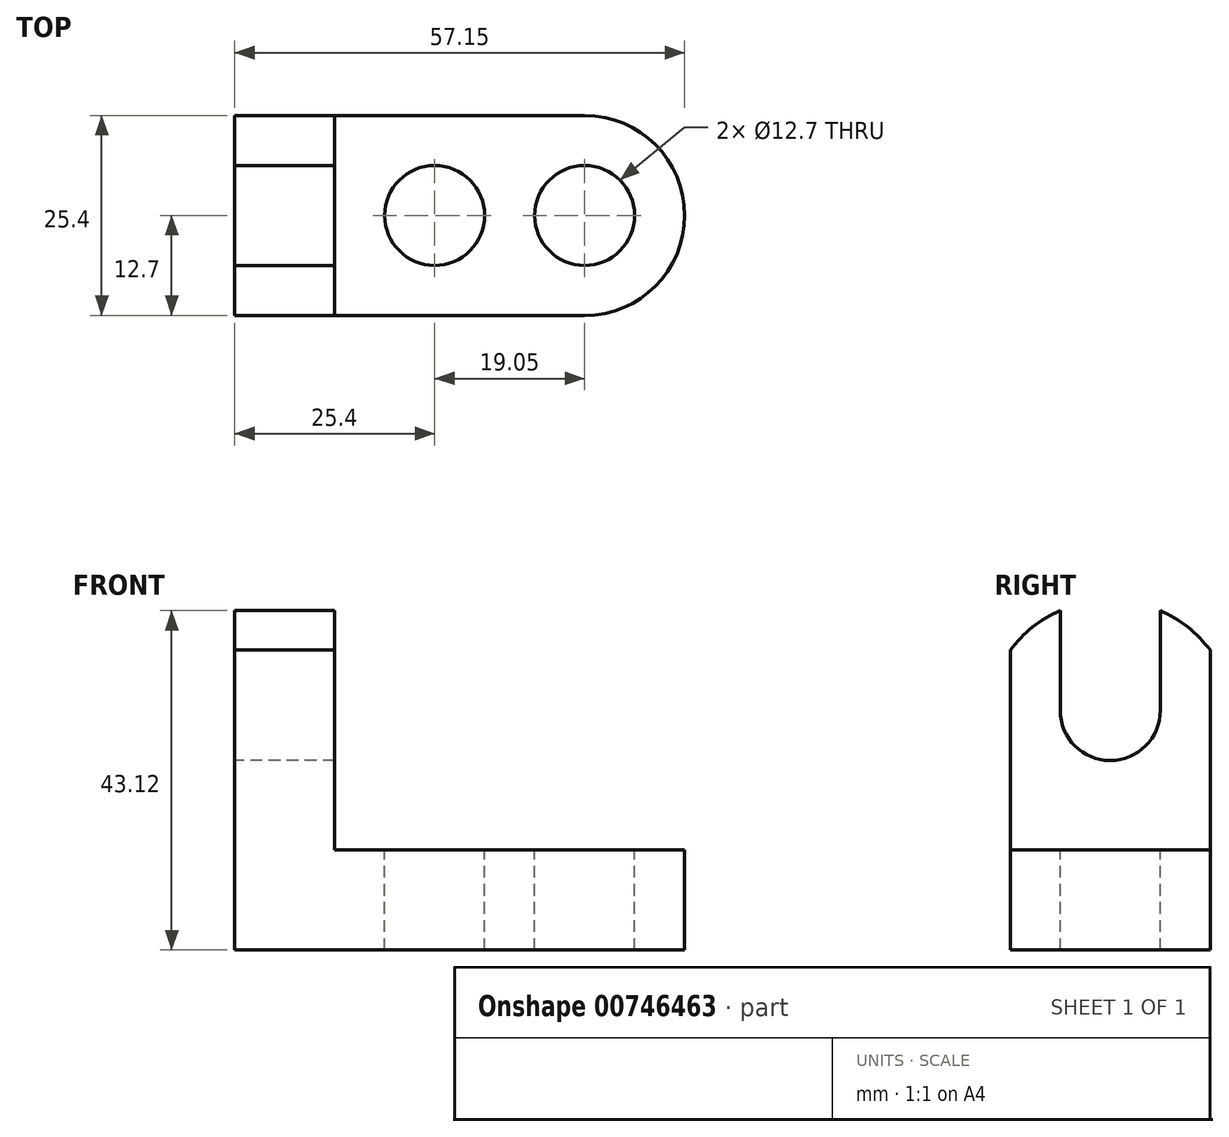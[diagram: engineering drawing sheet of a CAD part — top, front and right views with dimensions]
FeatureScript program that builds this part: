
annotation { "Feature Type Name" : "Feature", "Feature Type Description" : "" }
export const myFeature = defineFeature(function(context is Context, id is Id, definition is map)
    precondition{}
    {
        {
            var Q0;
            Q0=qCreatedBy(makeId("Front.planeOp"),FACE);
            var sketch = newSketch(context, id + "F0", { "sketchPlane" : qUnion([Q0])});
            skLineSegment(sketch, "E0", {"start": v(0, 0) * mm, "end": v(44.45, 0) * mm});
            skLineSegment(sketch, "E1", {"start": v(44.45, 0) * mm, "end": v(44.45, 12.7) * mm});
            skLineSegment(sketch, "E2", {"start": v(44.45, 12.7) * mm, "end": v(12.7, 12.7) * mm});
            skLineSegment(sketch, "E3", {"start": v(12.7, 12.7) * mm, "end": v(12.7, 38.1) * mm});
            skLineSegment(sketch, "E4", {"start": v(12.7, 38.1) * mm, "end": v(0, 38.1) * mm});
            skLineSegment(sketch, "E5", {"start": v(0, 38.1) * mm, "end": v(0, 0) * mm});
            skSolve(sketch);
        }
        {
            var Q0;
            Q0=makeQuery(id+"F0.imprint","IMPRINT",FACE,{"disambiguationData":[TD([[makeQuery(id+"F0.imprint","IMPRINT",EDGE,{"derivedFrom":sQuery(id+"F0.wireOp",EDGE,"E0")}),1.0]])]});
            extrude(context, id + "F1", {"entities" : qUnion([Q0]), "depth" : 25.4 * mm, "offsetDistance" : 25.4 * mm});
        }
        {
            var Q0;
            Q0=makeQuery(id+"F1.opExtrude","SWEPT_FACE",FACE,{"disambiguationData":[OSD([sQuery(id+"F0.wireOp",EDGE,"E5")])]});
            var sketch = newSketch(context, id + "F2", { "sketchPlane" : qUnion([Q0])});
            skArc(sketch, "E6", {"start": v(25.4, 38.1) * mm, "mid": v(12.7, 44.45) * mm, "end": v(0, 38.1) * mm});
            skLineSegment(sketch, "E7", {"start": v(6.35, 43.12) * mm, "end": v(6.35, 30.42) * mm});
            skLineSegment(sketch, "E8", {"start": v(6.35, 30.42) * mm, "end": v(19.05, 30.42) * mm});
            skLineSegment(sketch, "E9", {"start": v(19.05, 30.42) * mm, "end": v(19.05, 43.12) * mm});
            skArc(sketch, "E10", {"start": v(6.35, 30.42) * mm, "mid": v(12.7, 24.07) * mm, "end": v(19.05, 30.42) * mm});
            skSolve(sketch);
        }
        {
            var Q0;
            {var subQ0=sQuery(id+"F2.wireOp",EDGE,"E7");var subQ1=sQuery(id+"F2.wireOp",EDGE,"E6");var subQ2=makeQuery(id+"F2.imprint","INTERSECT",VERTEX,{"derivedFrom":[subQ1,subQ0]});Q0=makeQuery(id+"F2.imprint","IMPRINT",FACE,{"disambiguationData":[TD([[makeQuery(id+"F2.imprint","IMPRINT",EDGE,{"disambiguationData":[TD([[subQ2,1.0]])],"derivedFrom":subQ1}),1.0]])]});}
            var Q1;
            {var subQ1=sQuery(id+"F2.wireOp",EDGE,"E8");Q1=makeQuery(id+"F2.imprint","IMPRINT",FACE,{"disambiguationData":[TD([[makeQuery(id+"F2.imprint","IMPRINT",EDGE,{"derivedFrom":subQ1}),1.0]])]});}
            var Q2;
            Q2=makeQuery(id+"F2.imprint","IMPRINT",FACE,{"disambiguationData":[TD([[makeQuery(id+"F2.imprint","IMPRINT",EDGE,{"derivedFrom":sQuery(id+"F2.wireOp",EDGE,"E8")}),-1.0]])]});
            extrude(context, id + "F3", {"entities" : qUnion([Q0, Q1, Q2]), "operationType" : NewBodyOperationType.REMOVE, "oppositeDirection" : true, "depth" : 12.7 * mm, "offsetDistance" : 25.4 * mm});
        }
        {
            var Q0;
            {var subQ0=sQuery(id+"F2.wireOp",EDGE,"E6");var subQ4=sQuery(id+"F2.wireOp",EDGE,"E7");var subQ5=makeQuery(id+"F2.imprint","INTERSECT",VERTEX,{"derivedFrom":[subQ0,subQ4]});Q0=makeQuery(id+"F2.imprint","IMPRINT",FACE,{"disambiguationData":[TD([[makeQuery(id+"F2.imprint","IMPRINT",EDGE,{"disambiguationData":[TD([[subQ5,-1.0]])],"derivedFrom":subQ4}),-1.0]])]});}
            var Q1;
            {var subQ0=sQuery(id+"F2.wireOp",EDGE,"E6");var subQ4=sQuery(id+"F2.wireOp",EDGE,"E9");var subQ5=makeQuery(id+"F2.imprint","INTERSECT",VERTEX,{"derivedFrom":[subQ0,subQ4]});Q1=makeQuery(id+"F2.imprint","IMPRINT",FACE,{"disambiguationData":[TD([[makeQuery(id+"F2.imprint","IMPRINT",EDGE,{"disambiguationData":[TD([[subQ5,1.0]])],"derivedFrom":subQ4}),-1.0]])]});}
            extrude(context, id + "F4", {"entities" : qUnion([Q0, Q1]), "operationType" : NewBodyOperationType.ADD, "oppositeDirection" : true, "depth" : 12.7 * mm, "offsetDistance" : 25.4 * mm});
        }
        {
            var Q0;
            Q0=makeQuery(id+"F1.opExtrude","SWEPT_FACE",FACE,{"disambiguationData":[OSD([sQuery(id+"F0.wireOp",EDGE,"E2")])]});
            var sketch = newSketch(context, id + "F5", { "sketchPlane" : qUnion([Q0])});
            skArc(sketch, "E11", {"start": v(44.45, -25.4) * mm, "mid": v(57.15, -12.7) * mm, "end": v(44.45, 0) * mm});
            skCircle(sketch, "E12", {"center": v(44.45, -12.7) * mm, "radius": 6.35 * mm});
            skCircle(sketch, "E13", {"center": v(25.4, -12.7) * mm, "radius": 6.35 * mm});
            skSolve(sketch);
        }
        {
            var Q0;
            {var subQ0=sQuery(id+"F5.wireOp",EDGE,"E12");var subQ1=makeQuery(id+"F1.opExtrude","SWEPT_EDGE",EDGE,{"disambiguationData":[OSD([sQuery(id+"F0.wireOp",EDGE,"E1"),sQuery(id+"F0.wireOp",EDGE,"E2")])]});var subQ2=makeQuery(id+"F5.imprint","INTERSECT",VERTEX,{"disambiguationData":[OD(0.0)],"derivedFrom":[subQ1,subQ0]});Q0=makeQuery(id+"F5.imprint","IMPRINT",FACE,{"disambiguationData":[TD([[makeQuery(id+"F5.imprint","IMPRINT",EDGE,{"disambiguationData":[TD([[subQ2,1.0]])],"derivedFrom":subQ0}),1.0]])]});}
            var Q1;
            {var subQ0=sQuery(id+"F5.wireOp",EDGE,"E12");var subQ1=makeQuery(id+"F1.opExtrude","SWEPT_EDGE",EDGE,{"disambiguationData":[OSD([sQuery(id+"F0.wireOp",EDGE,"E1"),sQuery(id+"F0.wireOp",EDGE,"E2")])]});var subQ2=makeQuery(id+"F5.imprint","INTERSECT",VERTEX,{"disambiguationData":[OD(0.0)],"derivedFrom":[subQ1,subQ0]});Q1=makeQuery(id+"F5.imprint","IMPRINT",FACE,{"disambiguationData":[TD([[makeQuery(id+"F5.imprint","IMPRINT",EDGE,{"disambiguationData":[TD([[subQ2,-1.0]])],"derivedFrom":subQ0}),1.0]])]});}
            var Q2;
            Q2=makeQuery(id+"F5.imprint","IMPRINT",FACE,{"disambiguationData":[TD([[makeQuery(id+"F5.imprint","IMPRINT",EDGE,{"derivedFrom":sQuery(id+"F5.wireOp",EDGE,"E13")}),1.0]])]});
            extrude(context, id + "F6", {"entities" : qUnion([Q0, Q1, Q2]), "operationType" : NewBodyOperationType.REMOVE, "oppositeDirection" : true, "depth" : 25.4 * mm, "offsetDistance" : 25.4 * mm});
        }
        {
            var Q0;
            {var subQ0=sQuery(id+"F5.wireOp",EDGE,"E11");Q0=makeQuery(id+"F5.imprint","IMPRINT",FACE,{"disambiguationData":[TD([[makeQuery(id+"F5.imprint","IMPRINT",EDGE,{"derivedFrom":subQ0}),1.0]])]});}
            extrude(context, id + "F7", {"entities" : qUnion([Q0]), "operationType" : NewBodyOperationType.ADD, "oppositeDirection" : true, "depth" : 12.7 * mm, "offsetDistance" : 25.4 * mm});
        }
    });
